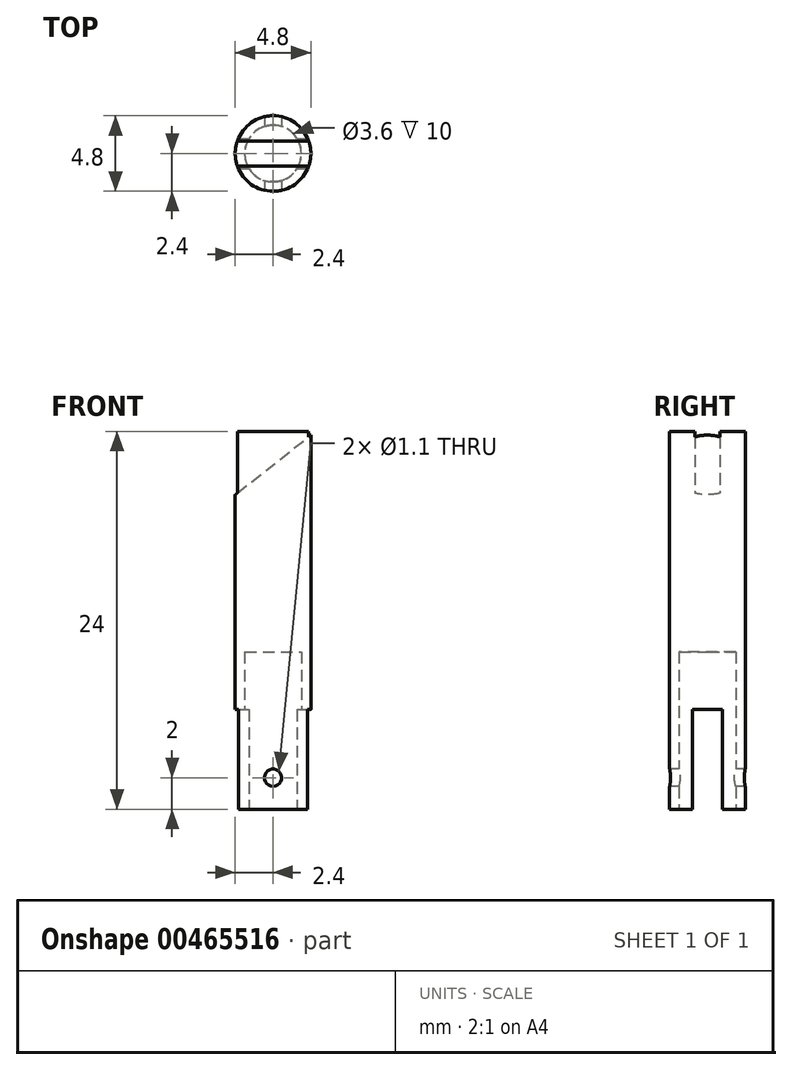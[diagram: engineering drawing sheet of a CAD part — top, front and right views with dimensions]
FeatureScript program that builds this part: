
annotation { "Feature Type Name" : "Feature", "Feature Type Description" : "" }
export const myFeature = defineFeature(function(context is Context, id is Id, definition is map)
    precondition{}
    {
        {
            var Q0;
            Q0=qCreatedBy(makeId("Top.planeOp"),FACE);
            var sketch = newSketch(context, id + "F0", { "sketchPlane" : qUnion([Q0])});
            skCircle(sketch, "E0", {"center": v(0, 0) * mm, "radius": 2.4 * mm});
            skSolve(sketch);
        }
        {
            var Q0;
            Q0 = qSketchRegion(id + "F0", true);
            extrude(context, id + "F1", {"entities" : qUnion([Q0]), "depth" : 24 * mm});
        }
        {
            var Q0;
            Q0=makeQuery(id+"F1.opExtrude","CAP_FACE",FACE,{"disambiguationData":[OSD([sQuery(id+"F0.wireOp",EDGE,"E0")])],"isStart":true});
            var sketch = newSketch(context, id + "F2", { "sketchPlane" : qUnion([Q0])});
            skCircle(sketch, "E1", {"center": v(0, 0) * mm, "radius": 1.8 * mm});
            skSolve(sketch);
        }
        {
            var Q0;
            Q0 = qSketchRegion(id + "F2", true);
            extrude(context, id + "F3", {"entities" : qUnion([Q0]), "operationType" : NewBodyOperationType.REMOVE, "oppositeDirection" : true, "depth" : 10 * mm});
        }
        {
            var Q0;
            Q0=qCreatedBy(makeId("Right.planeOp"),FACE);
            var sketch = newSketch(context, id + "F4", { "sketchPlane" : qUnion([Q0])});
            skLineSegment(sketch, "E2", {"start": v(0.95, 0) * mm, "end": v(0.95, 6.33) * mm});
            skLineSegment(sketch, "E3", {"start": v(0.95, 6.33) * mm, "end": v(0, 6.33) * mm});
            skLineSegment(sketch, "E4.MirrorCS", {"start": v(-0.95, 0) * mm, "end": v(-0.95, 6.33) * mm});
            skLineSegment(sketch, "E5.MirrorCS", {"start": v(-0.95, 6.33) * mm, "end": v(0, 6.33) * mm});
            skLineSegment(sketch, "E6", {"start": v(-0.95, 0) * mm, "end": v(0.95, 0) * mm});
            skSolve(sketch);
        }
        {
            var Q0;
            Q0 = qSketchRegion(id + "F4", true);
            extrude(context, id + "F5", {"entities" : qUnion([Q0]), "operationType" : NewBodyOperationType.REMOVE, "oppositeDirection" : true, "depth" : 25 * mm, "hasSecondDirection" : true, "secondDirectionOppositeDirection" : false, "secondDirectionDepth" : 25 * mm});
        }
        {
            var Q0;
            Q0=qCreatedBy(makeId("Front.planeOp"),FACE);
            var sketch = newSketch(context, id + "F6", { "sketchPlane" : qUnion([Q0])});
            skLineSegment(sketch, "E7", {"start": v(-2.5, 24) * mm, "end": v(-2.5, 19.9) * mm});
            skLineSegment(sketch, "E8", {"start": v(-2.5, 19.9) * mm, "end": v(2.7, 24) * mm});
            skLineSegment(sketch, "E9", {"start": v(2.7, 24) * mm, "end": v(-2.5, 24) * mm});
            skLineSegment(sketch, "E10.0", {"start": v(-2.4, 24) * mm, "end": v(2.4, 24) * mm});
            skSolve(sketch);
        }
        {
            var Q0;
            Q0 = qSketchRegion(id + "F6", true);
            extrude(context, id + "F7", {"entities" : qUnion([Q0]), "operationType" : NewBodyOperationType.REMOVE, "depth" : 0.8 * mm, "hasSecondDirection" : true, "secondDirectionOppositeDirection" : true, "secondDirectionDepth" : 0.8 * mm});
        }
        {
            var Q0;
            Q0=qCreatedBy(makeId("Front.planeOp"),FACE);
            var sketch = newSketch(context, id + "F8", { "sketchPlane" : qUnion([Q0])});
            skCircle(sketch, "E11", {"center": v(0, 2) * mm, "radius": 0.55 * mm});
            skSolve(sketch);
        }
        {
            var Q0;
            Q0 = qSketchRegion(id + "F8", true);
            extrude(context, id + "F9", {"entities" : qUnion([Q0]), "operationType" : NewBodyOperationType.REMOVE, "endBound" : BoundingType.THROUGH_ALL, "oppositeDirection" : true, "depth" : 25 * mm, "hasSecondDirection" : true, "secondDirectionBound" : SecondDirectionBoundingType.THROUGH_ALL, "secondDirectionOppositeDirection" : false, "secondDirectionDepth" : 25 * mm});
        }
    });
